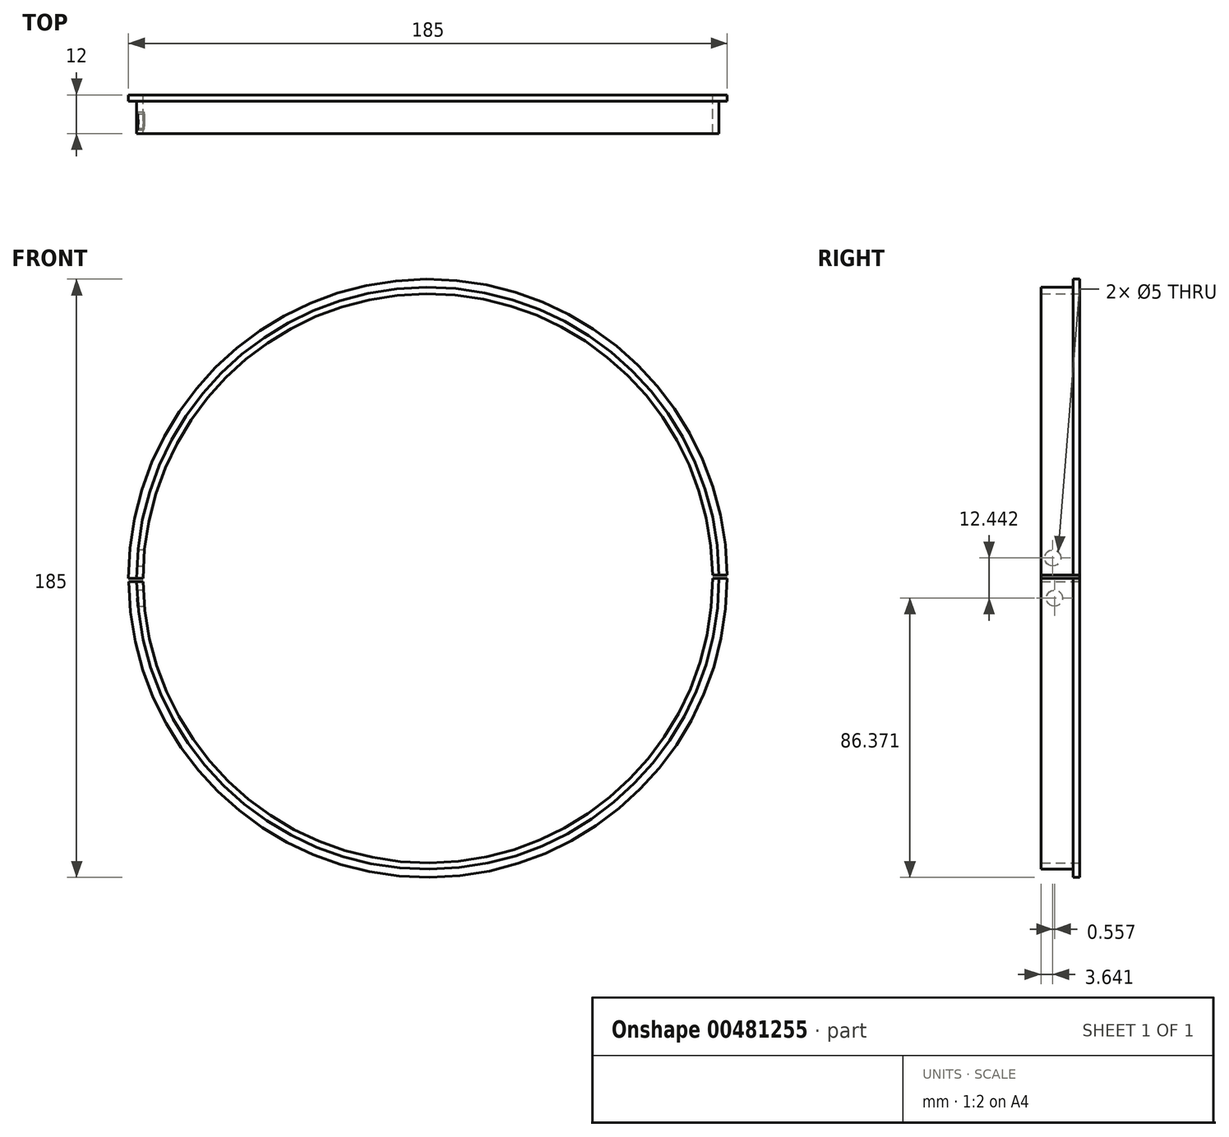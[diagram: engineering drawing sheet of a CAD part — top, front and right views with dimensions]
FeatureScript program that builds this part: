
annotation { "Feature Type Name" : "Feature", "Feature Type Description" : "" }
export const myFeature = defineFeature(function(context is Context, id is Id, definition is map)
    precondition{}
    {
        {
            var Q0;
            Q0=qCreatedBy(makeId("Front.planeOp"),FACE);
            var sketch = newSketch(context, id + "F0", { "sketchPlane" : qUnion([Q0])});
            skCircle(sketch, "E0", {"center": v(0, 0) * mm, "radius": 90 * mm});
            skCircle(sketch, "E1", {"center": v(0, 0) * mm, "radius": 88 * mm});
            skSolve(sketch);
        }
        {
            var Q0;
            Q0=makeQuery(id+"F0.imprint","IMPRINT",FACE,{"disambiguationData":[TD([[makeQuery(id+"F0.imprint","IMPRINT",EDGE,{"derivedFrom":sQuery(id+"F0.wireOp",EDGE,"E0")}),1.0]])]});
            extrude(context, id + "F1", {"entities" : qUnion([Q0]), "depth" : 10 * mm, "offsetDistance" : 25 * mm});
        }
        {
            var Q0;
            Q0=qCreatedBy(makeId("Front.planeOp"),FACE);
            var sketch = newSketch(context, id + "F2", { "sketchPlane" : qUnion([Q0])});
            skCircle(sketch, "E2", {"center": v(0, 0) * mm, "radius": 92.5 * mm});
            skCircle(sketch, "E3", {"center": v(0, 0) * mm, "radius": 88 * mm});
            skSolve(sketch);
        }
        {
            var Q0;
            Q0 = qSketchRegion(id + "F2", true);
            extrude(context, id + "F3", {"entities" : qUnion([Q0]), "operationType" : NewBodyOperationType.ADD, "oppositeDirection" : true, "depth" : 2 * mm, "offsetDistance" : 25 * mm});
        }
        {
            var Q0;
            Q0=qCreatedBy(makeId("Front.planeOp"),FACE);
            var sketch = newSketch(context, id + "F4", { "sketchPlane" : qUnion([Q0])});
            skPoint(sketch, "E4.startSnap0", {"position": v(45.45, 0) * mm});
            skLineSegment(sketch, "E5.left", {"start": v(-42.7, 0) * mm, "end": v(-42.7, 0.5) * mm});
            skLineSegment(sketch, "E5.right", {"start": v(-48.93, 0) * mm, "end": v(-48.93, 0.5) * mm});
            skLineSegment(sketch, "E6", {"start": v(29.11, -29.73) * mm, "end": v(29.44, -29.35) * mm});
            skLineSegment(sketch, "E7", {"start": v(36.17, -35.76) * mm, "end": v(36.48, -35.37) * mm});
            skLineSegment(sketch, "E8.bottom", {"start": v(79.78, 1) * mm, "end": v(104.17, 1) * mm});
            skLineSegment(sketch, "E8.top", {"start": v(79.78, 0) * mm, "end": v(104.17, 0) * mm});
            skLineSegment(sketch, "E8.left", {"start": v(79.78, 1) * mm, "end": v(79.78, 0) * mm});
            skLineSegment(sketch, "E8.right", {"start": v(104.17, 1) * mm, "end": v(104.17, 0) * mm});
            skLineSegment(sketch, "E9.bottom", {"start": v(-82.36, -1) * mm, "end": v(-98.7, -1) * mm});
            skLineSegment(sketch, "E9.top", {"start": v(-82.36, 0) * mm, "end": v(-98.7, 0) * mm});
            skLineSegment(sketch, "E9.left", {"start": v(-82.36, -1) * mm, "end": v(-82.36, 0) * mm});
            skLineSegment(sketch, "E9.right", {"start": v(-98.7, -1) * mm, "end": v(-98.7, 0) * mm});
            skSolve(sketch);
        }
        {
            var Q0;
            Q0=qCreatedBy(makeId("Right.planeOp"),FACE);
            var sketch = newSketch(context, id + "F5", { "sketchPlane" : qUnion([Q0])});
            skCircle(sketch, "E10", {"center": v(-5.8, -6.13) * mm, "radius": 1 * mm});
            skCircle(sketch, "E11", {"center": v(-6.36, 6.31) * mm, "radius": 1 * mm});
            skSolve(sketch);
        }
        {
            var Q0;
            Q0=sQuery(id+"F5.wireOp",VERTEX,"E11.center");
            var Q1;
            Q1=sQuery(id+"F5.wireOp",VERTEX,"E10.center");
            var Q2;
            Q2=makeQuery(id+"FXC9OTLwf98COCe_2.boolean.opBoolean","SPLIT",BODY,{"disambiguationData":[OD(0.0)],"derivedFrom":makeQuery(id+"F1.opExtrude","SWEPT_BODY",BODY,{"disambiguationData":[OSD([sQuery(id+"F0.wireOp",EDGE,"E0"),sQuery(id+"F0.wireOp",EDGE,"E1")])]})});
            var Q3;
            Q3=makeQuery(id+"FXC9OTLwf98COCe_2.boolean.opBoolean","SPLIT",BODY,{"disambiguationData":[OD(1.0)],"derivedFrom":makeQuery(id+"F1.opExtrude","SWEPT_BODY",BODY,{"disambiguationData":[OSD([sQuery(id+"F0.wireOp",EDGE,"E0"),sQuery(id+"F0.wireOp",EDGE,"E1")])]})});
            hole(context, id + "F6", {"style" : HoleStyle.SIMPLE, "endStyle" : HoleEndStyle.THROUGH, "holeDiameter" : 5 * mm, "tappedDepth" : 12 * mm, "tapClearance" : 3, "locations" : qUnion([Q0, Q1]), "scope" : qUnion([Q2, Q3])});
        }
        {
            var Q0;
            Q0 = qSketchRegion(id + "F4", true);
            extrude(context, id + "F7", {"entities" : qUnion([Q0]), "operationType" : NewBodyOperationType.REMOVE, "depth" : 25 * mm});
        }
        {
            var Q0;
            Q0 = qSketchRegion(id + "F4", true);
            extrude(context, id + "F8", {"entities" : qUnion([Q0]), "operationType" : NewBodyOperationType.REMOVE, "oppositeDirection" : true, "depth" : 25 * mm});
        }
    });
